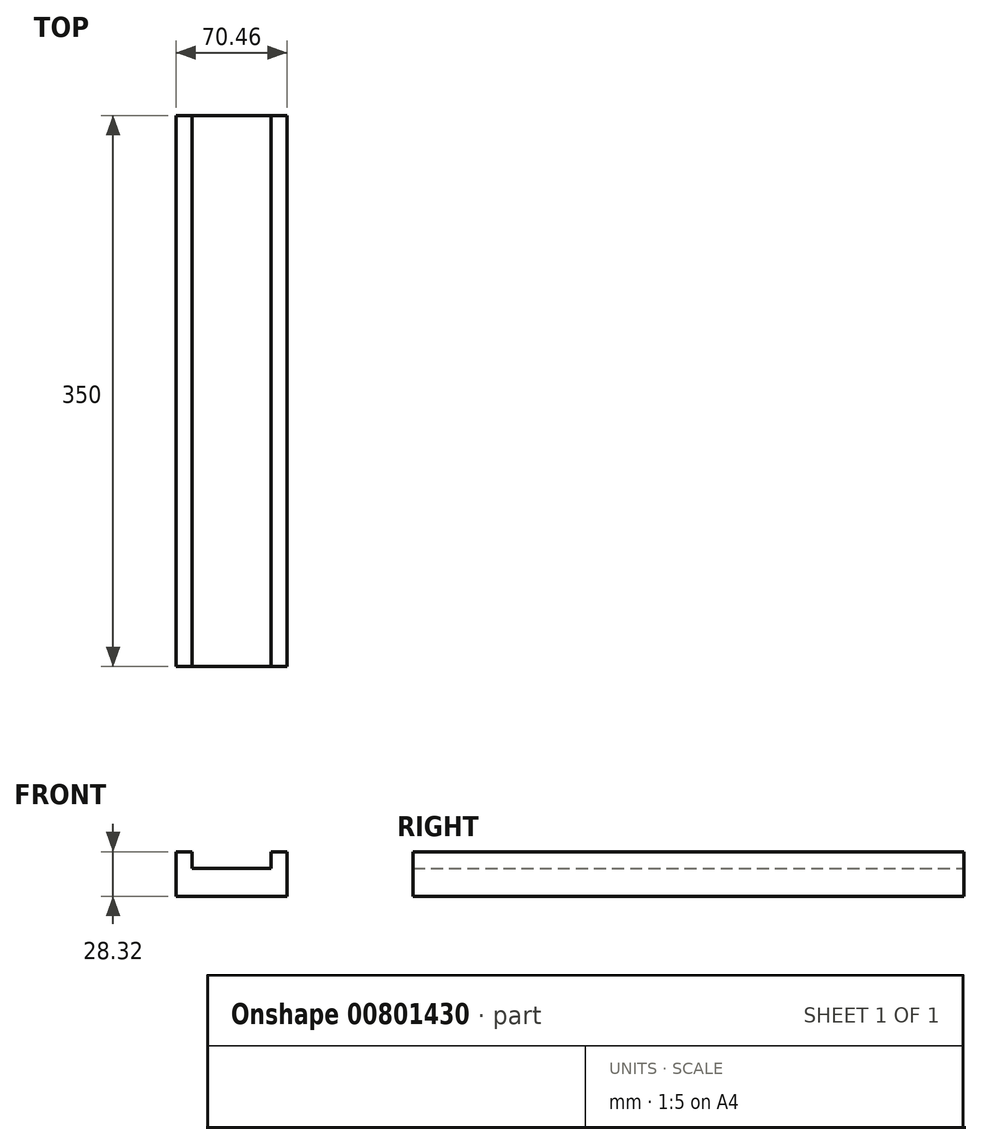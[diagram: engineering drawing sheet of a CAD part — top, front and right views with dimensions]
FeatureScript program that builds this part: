
annotation { "Feature Type Name" : "Feature", "Feature Type Description" : "" }
export const myFeature = defineFeature(function(context is Context, id is Id, definition is map)
    precondition{}
    {
        {
            var Q0;
            Q0=qCreatedBy(makeId("Front.planeOp"),FACE);
            var sketch = newSketch(context, id + "F0", { "sketchPlane" : qUnion([Q0])});
            skLineSegment(sketch, "E0.bottom", {"start": v(-33.16, 0) * mm, "end": v(37.3, 0) * mm});
            skLineSegment(sketch, "E0.top", {"start": v(-33.16, 28.32) * mm, "end": v(-22.93, 28.32) * mm});
            skLineSegment(sketch, "E0.left", {"start": v(-33.16, 0) * mm, "end": v(-33.16, 28.32) * mm});
            skLineSegment(sketch, "E0.right", {"start": v(37.3, 0) * mm, "end": v(37.3, 28.32) * mm});
            skLineSegment(sketch, "E1.top", {"start": v(-22.93, 17.55) * mm, "end": v(27.08, 17.55) * mm});
            skLineSegment(sketch, "E1.left", {"start": v(-22.93, 28.32) * mm, "end": v(-22.93, 17.55) * mm});
            skLineSegment(sketch, "E1.right", {"start": v(27.08, 28.32) * mm, "end": v(27.08, 17.55) * mm});
            skLineSegment(sketch, "E2.trimOffspring", {"start": v(27.08, 28.32) * mm, "end": v(37.3, 28.32) * mm});
            skSolve(sketch);
        }
        {
            var Q0;
            Q0 = qSketchRegion(id + "F0", true);
            extrude(context, id + "F1", {"entities" : qUnion([Q0]), "depth" : 350 * mm, "offsetDistance" : 25 * mm});
        }
    });
